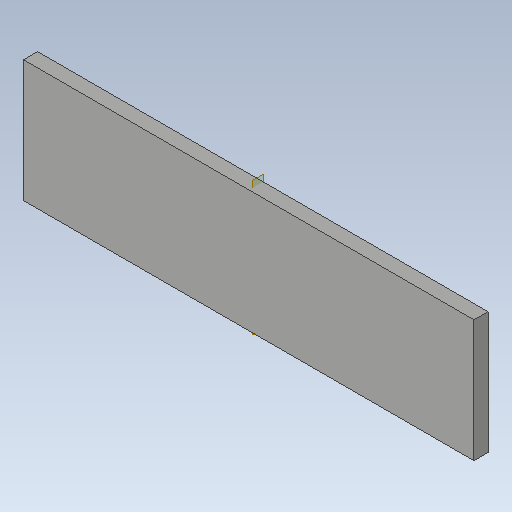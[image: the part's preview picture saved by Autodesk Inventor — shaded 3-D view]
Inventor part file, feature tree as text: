
AUTODESK INVENTOR PART (.ipt)
format: ipt  version: 2020.1 (Build 241239000, 239)  size: 127,488 bytes
history: native  units: mm
features: other x6, plane x1, sheet_metal_op x1, sketch x1, reference x1
ambient origin geometry x8: Origin, YZ Plane, XZ Plane, XY Plane, X Axis, Y Axis, Z Axis, Center Point
bodies: Solid1 (feature_tree)
feature tree (10):
  plane  "Work Plane1"
  sheet_metal_op  "Face1"
  other  "midtplan"
  sketch  "Sketch1"  dims[d7=3.0mm d8=12.0mm d9=12.0mm d10=26.0mm]
  reference  "Reference1"
  other  "Plate1"
  parser-record x1  (decoder bookkeeping rows leaked as tree rows — omitted from the tree; the rows remain in map.json)
  other  "modul.iam"
  other  "plade:1"
  other  "Definition1"
note: 1 file-system path scrubbed to <path> (originals preserved in map.json)
